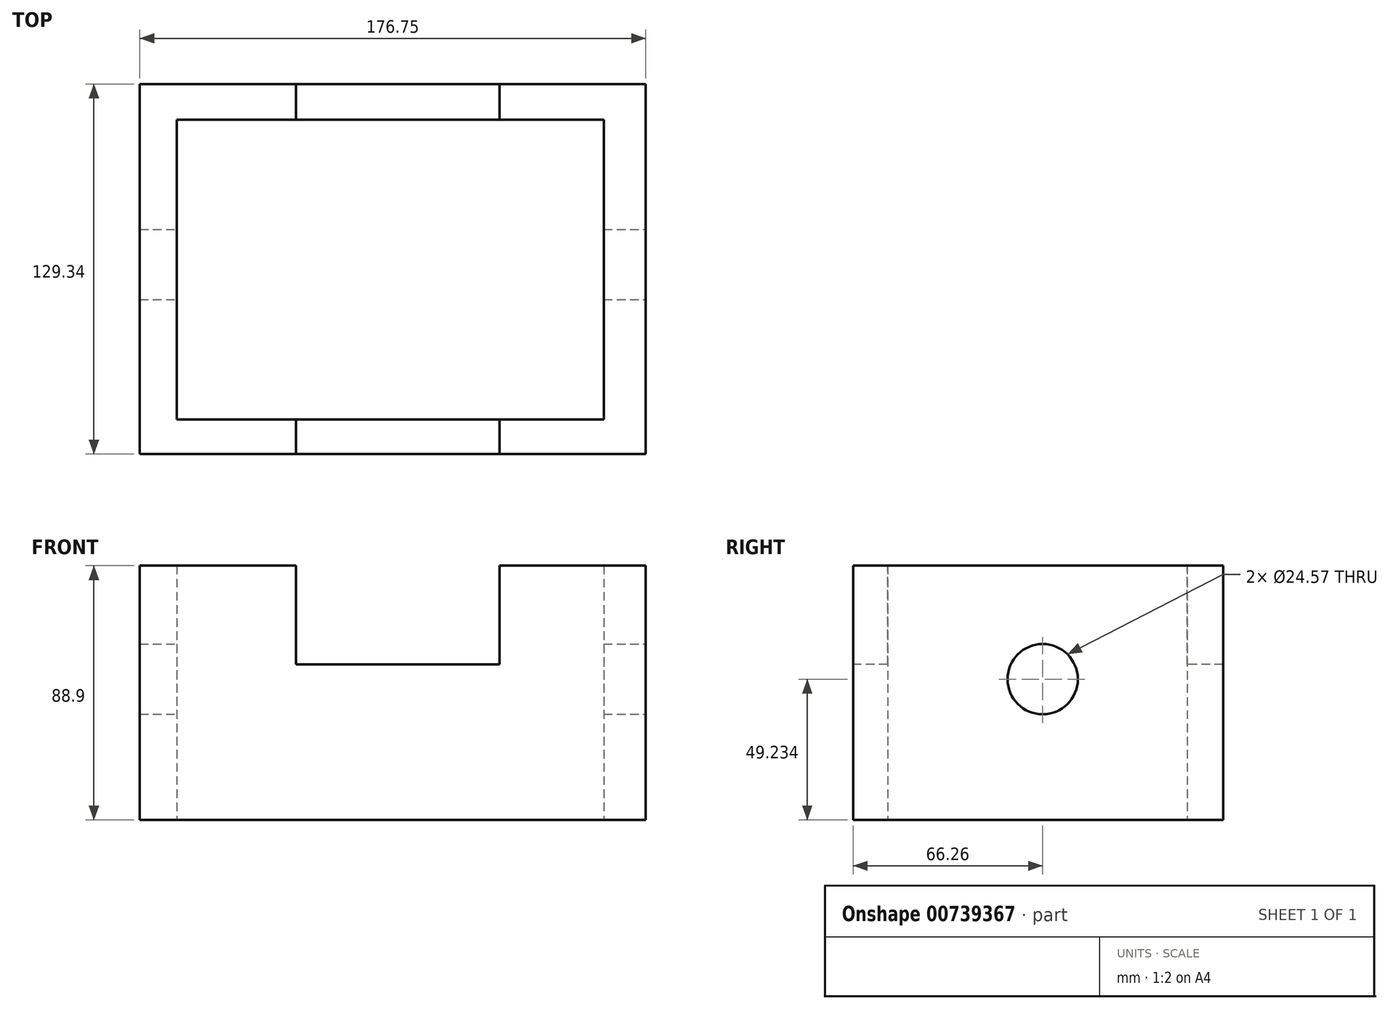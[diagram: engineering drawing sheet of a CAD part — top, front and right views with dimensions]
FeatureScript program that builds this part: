
annotation { "Feature Type Name" : "Feature", "Feature Type Description" : "" }
export const myFeature = defineFeature(function(context is Context, id is Id, definition is map)
    precondition{}
    {
        {
            var Q0;
            Q0=qCreatedBy(makeId("Top.planeOp"),FACE);
            var sketch = newSketch(context, id + "F0", { "sketchPlane" : qUnion([Q0])});
            skLineSegment(sketch, "E0.bottom", {"start": v(66.2, -66.26) * mm, "end": v(-110.55, -66.26) * mm});
            skLineSegment(sketch, "E0.top", {"start": v(66.2, 63.08) * mm, "end": v(-110.55, 63.08) * mm});
            skLineSegment(sketch, "E0.left", {"start": v(66.2, -66.26) * mm, "end": v(66.2, 63.08) * mm});
            skLineSegment(sketch, "E0.right", {"start": v(-110.55, -66.26) * mm, "end": v(-110.55, 63.08) * mm});
            skLineSegment(sketch, "E1.bottom", {"start": v(-97.6, -54.16) * mm, "end": v(51.57, -54.16) * mm});
            skLineSegment(sketch, "E1.top", {"start": v(-97.6, 50.56) * mm, "end": v(51.57, 50.56) * mm});
            skLineSegment(sketch, "E1.left", {"start": v(-97.6, -54.16) * mm, "end": v(-97.6, 50.56) * mm});
            skLineSegment(sketch, "E1.right", {"start": v(51.57, -54.16) * mm, "end": v(51.57, 50.56) * mm});
            skSolve(sketch);
        }
        {
            var Q0;
            Q0=makeQuery(id+"F0.imprint","IMPRINT",FACE,{"disambiguationData":[TD([[makeQuery(id+"F0.imprint","IMPRINT",EDGE,{"derivedFrom":sQuery(id+"F0.wireOp",EDGE,"E0.bottom")}),-1.0]])]});
            extrude(context, id + "F1", {"entities" : qUnion([Q0]), "depth" : 88.9 * mm, "offsetDistance" : 25.4 * mm});
        }
        {
            var Q0;
            Q0=makeQuery(id+"F1.opExtrude","SWEPT_FACE",FACE,{"disambiguationData":[OSD([sQuery(id+"F0.wireOp",EDGE,"E0.bottom")])]});
            var sketch = newSketch(context, id + "F2", { "sketchPlane" : qUnion([Q0])});
            skLineSegment(sketch, "E2.bottom", {"start": v(-55.94, 88.9) * mm, "end": v(15.23, 88.9) * mm});
            skLineSegment(sketch, "E2.top", {"start": v(-55.94, 54.4) * mm, "end": v(15.23, 54.4) * mm});
            skLineSegment(sketch, "E2.left", {"start": v(-55.94, 88.9) * mm, "end": v(-55.94, 54.4) * mm});
            skLineSegment(sketch, "E2.right", {"start": v(15.23, 88.9) * mm, "end": v(15.23, 54.4) * mm});
            skSolve(sketch);
        }
        {
            var Q0;
            Q0=makeQuery(id+"F2.imprint","IMPRINT",FACE,{"disambiguationData":[TD([[makeQuery(id+"F2.imprint","IMPRINT",EDGE,{"derivedFrom":sQuery(id+"F2.wireOp",EDGE,"E2.bottom")}),1.0]])]});
            extrude(context, id + "F3", {"entities" : qUnion([Q0]), "operationType" : NewBodyOperationType.REMOVE, "oppositeDirection" : true, "depth" : 152.4 * mm, "offsetDistance" : 25.4 * mm});
        }
        {
            var Q0;
            Q0=makeQuery(id+"F1.opExtrude","SWEPT_FACE",FACE,{"disambiguationData":[OSD([sQuery(id+"F0.wireOp",EDGE,"E0.left")])]});
            var sketch = newSketch(context, id + "F4", { "sketchPlane" : qUnion([Q0])});
            skCircle(sketch, "E3", {"center": v(0, 49.23) * mm, "radius": 12.28 * mm});
            skSolve(sketch);
        }
        {
            var Q0;
            Q0=makeQuery(id+"F4.imprint","IMPRINT",FACE,{"disambiguationData":[TD([[makeQuery(id+"F4.imprint","IMPRINT",EDGE,{"derivedFrom":sQuery(id+"F4.wireOp",EDGE,"E3")}),1.0]])]});
            extrude(context, id + "F5", {"entities" : qUnion([Q0]), "operationType" : NewBodyOperationType.REMOVE, "oppositeDirection" : true, "depth" : 254 * mm, "offsetDistance" : 25.4 * mm});
        }
    });
